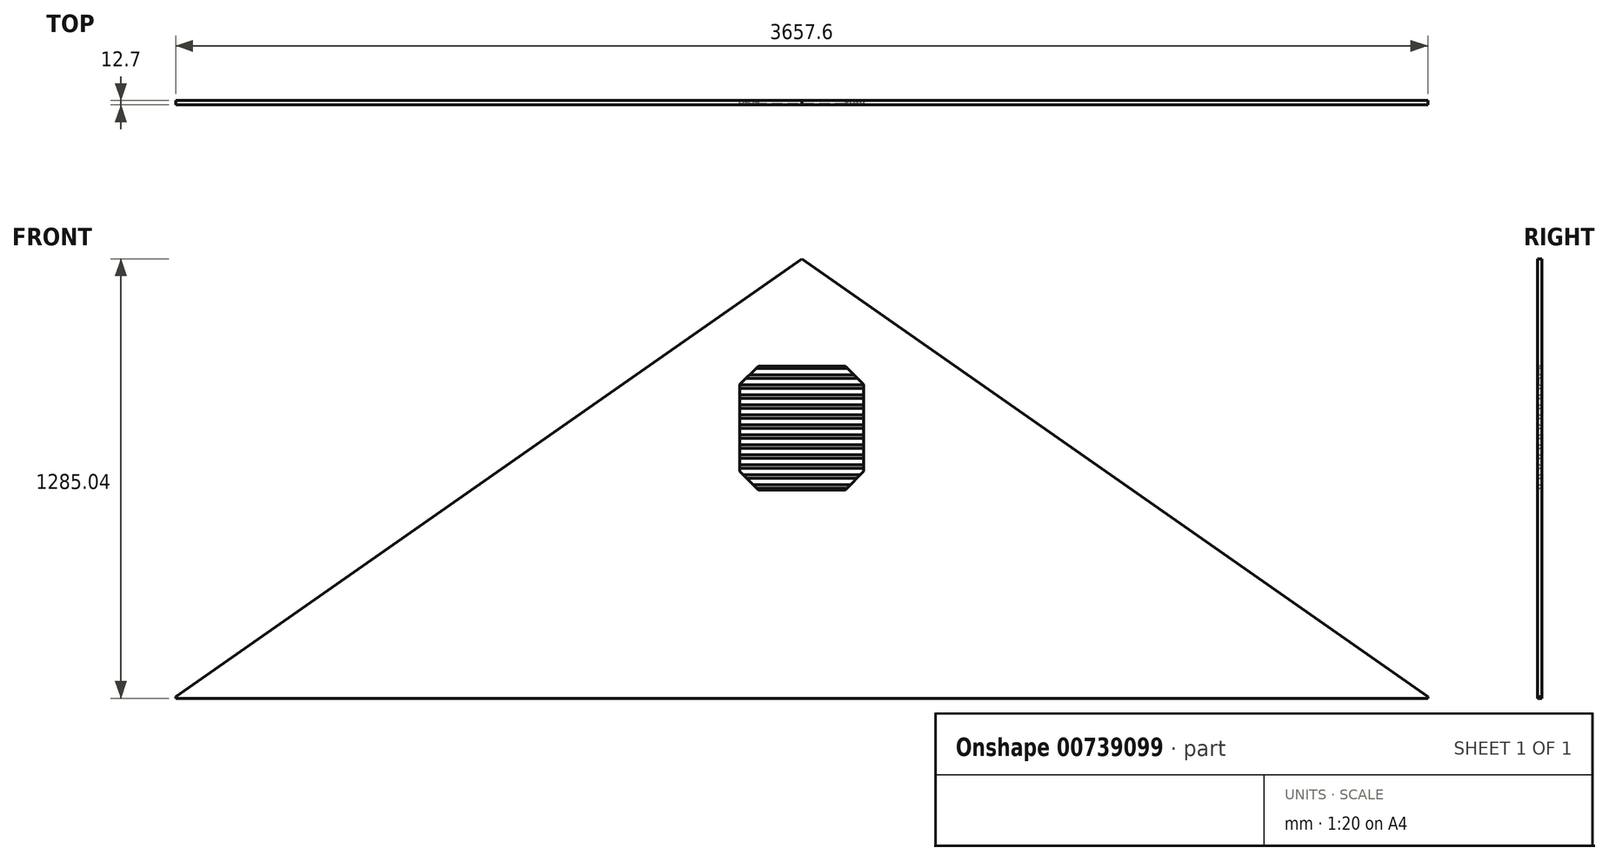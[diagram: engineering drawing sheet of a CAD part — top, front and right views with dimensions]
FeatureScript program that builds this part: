
annotation { "Feature Type Name" : "Feature", "Feature Type Description" : "" }
export const myFeature = defineFeature(function(context is Context, id is Id, definition is map)
    precondition{}
    {
        {
            var Q0;
            Q0=qCreatedBy(makeId("Front.planeOp"),FACE);
            var sketch = newSketch(context, id + "F0", { "sketchPlane" : qUnion([Q0])});
            skLineSegment(sketch, "E0", {"start": v(0, 0) * mm, "end": v(3657.6, 0) * mm});
            skLineSegment(sketch, "E1", {"start": v(3657.6, 0) * mm, "end": v(3657.6, 4.5) * mm});
            skLineSegment(sketch, "E2", {"start": v(3657.6, 4.5) * mm, "end": v(1828.8, 1285.04) * mm});
            skLineSegment(sketch, "E3", {"start": v(1828.8, 1285.04) * mm, "end": v(0, 4.5) * mm});
            skLineSegment(sketch, "E4", {"start": v(0, 4.5) * mm, "end": v(0, 0) * mm});
            skLineSegment(sketch, "E5", {"start": v(1828.8, 0) * mm, "end": v(1828.8, 1996.1) * mm});
            skSolve(sketch);
        }
        {
            var Q0;
            {var subQ4=sQuery(id+"F0.wireOp",EDGE,"E3");Q0=makeQuery(id+"F0.imprint","IMPRINT",FACE,{"disambiguationData":[TD([[makeQuery(id+"F0.imprint","IMPRINT",EDGE,{"derivedFrom":subQ4}),1.0]])]});}
            var Q1;
            {var subQ0=sQuery(id+"F0.wireOp",EDGE,"E1");Q1=makeQuery(id+"F0.imprint","IMPRINT",FACE,{"disambiguationData":[TD([[makeQuery(id+"F0.imprint","IMPRINT",EDGE,{"derivedFrom":subQ0}),1.0]])]});}
            extrude(context, id + "F1", {"entities" : qUnion([Q0, Q1]), "depth" : 12.7 * mm, "offsetDistance" : 25.4 * mm});
        }
        {
            var Q0;
            Q0=makeQuery(id+"F1.opExtrude","CAP_FACE",FACE,{"disambiguationData":[OSD([sQuery(id+"F0.wireOp",EDGE,"E0"),sQuery(id+"F0.wireOp",EDGE,"E1"),sQuery(id+"F0.wireOp",EDGE,"E2"),sQuery(id+"F0.wireOp",EDGE,"E3"),sQuery(id+"F0.wireOp",EDGE,"E4")])],"isStart":false});
            var sketch = newSketch(context, id + "F2", { "sketchPlane" : qUnion([Q0])});
            skLineSegment(sketch, "E6", {"start": v(1828.8, 1285.04) * mm, "end": v(1828.8, -385.73) * mm, "construction": true});
            skLineSegment(sketch, "E7", {"start": v(1701.8, 609.6) * mm, "end": v(1955.8, 609.6) * mm});
            skLineSegment(sketch, "E8", {"start": v(1955.8, 609.6) * mm, "end": v(2009.68, 663.48) * mm});
            skLineSegment(sketch, "E9", {"start": v(2009.68, 663.48) * mm, "end": v(2009.68, 917.48) * mm});
            skLineSegment(sketch, "E10", {"start": v(2009.68, 917.48) * mm, "end": v(1955.8, 971.36) * mm});
            skLineSegment(sketch, "E11", {"start": v(1955.8, 971.36) * mm, "end": v(1701.8, 971.36) * mm});
            skLineSegment(sketch, "E12", {"start": v(1701.8, 971.36) * mm, "end": v(1647.92, 917.48) * mm});
            skLineSegment(sketch, "E13", {"start": v(1647.92, 917.48) * mm, "end": v(1647.92, 663.48) * mm});
            skLineSegment(sketch, "E14", {"start": v(1647.92, 663.48) * mm, "end": v(1701.8, 609.6) * mm});
            skPoint(sketch, "E15", {"position": v(1828.8, 609.6) * mm});
            skLineSegment(sketch, "E16", {"start": v(1647.92, 790.48) * mm, "end": v(2046.19, 790.48) * mm});
            skSolve(sketch);
        }
        {
            var Q0;
            {var subQ1=sQuery(id+"F2.wireOp",EDGE,"E10");Q0=makeQuery(id+"F2.imprint","IMPRINT",FACE,{"disambiguationData":[TD([[makeQuery(id+"F2.imprint","IMPRINT",EDGE,{"derivedFrom":subQ1}),1.0]])]});}
            var Q1;
            Q1=makeQuery(id+"F2.imprint","IMPRINT",FACE,{"disambiguationData":[TD([[makeQuery(id+"F2.imprint","IMPRINT",EDGE,{"derivedFrom":sQuery(id+"F2.wireOp",EDGE,"E7")}),1.0]])]});
            extrude(context, id + "F3", {"entities" : qUnion([Q0, Q1]), "operationType" : NewBodyOperationType.REMOVE, "oppositeDirection" : true, "depth" : 89.66 * mm, "offsetDistance" : 25.4 * mm});
        }
        {
            var Q0;
            Q0=qCreatedBy(makeId("Front.planeOp"),FACE);
            var sketch = newSketch(context, id + "F4", { "sketchPlane" : qUnion([Q0])});
            skLineSegment(sketch, "E17.bottom", {"start": v(1524, 964.14) * mm, "end": v(2133.6, 964.14) * mm});
            skLineSegment(sketch, "E17.top", {"start": v(1524, 945.1) * mm, "end": v(2133.6, 945.1) * mm});
            skLineSegment(sketch, "E17.left", {"start": v(1524, 964.14) * mm, "end": v(1524, 945.1) * mm});
            skLineSegment(sketch, "E17.right", {"start": v(2133.6, 964.14) * mm, "end": v(2133.6, 945.1) * mm});
            skLineSegment(sketch, "E18.bottom", {"start": v(1524, 934.93) * mm, "end": v(2133.6, 934.93) * mm});
            skLineSegment(sketch, "E18.top", {"start": v(1524, 915.88) * mm, "end": v(2133.6, 915.88) * mm});
            skLineSegment(sketch, "E18.left", {"start": v(1524, 934.93) * mm, "end": v(1524, 915.88) * mm});
            skLineSegment(sketch, "E18.right", {"start": v(2133.6, 934.93) * mm, "end": v(2133.6, 915.88) * mm});
            skLineSegment(sketch, "E19.bottom", {"start": v(1524, 905.72) * mm, "end": v(2133.6, 905.72) * mm});
            skLineSegment(sketch, "E19.top", {"start": v(1524, 886.67) * mm, "end": v(2133.6, 886.67) * mm});
            skLineSegment(sketch, "E19.left", {"start": v(1524, 905.72) * mm, "end": v(1524, 886.67) * mm});
            skLineSegment(sketch, "E19.right", {"start": v(2133.6, 905.72) * mm, "end": v(2133.6, 886.67) * mm});
            skLineSegment(sketch, "E20.bottom", {"start": v(1524, 876.51) * mm, "end": v(2133.6, 876.51) * mm});
            skLineSegment(sketch, "E20.top", {"start": v(1524, 857.46) * mm, "end": v(2133.6, 857.46) * mm});
            skLineSegment(sketch, "E20.left", {"start": v(1524, 876.51) * mm, "end": v(1524, 857.46) * mm});
            skLineSegment(sketch, "E20.right", {"start": v(2133.6, 876.51) * mm, "end": v(2133.6, 857.46) * mm});
            skLineSegment(sketch, "E21.bottom", {"start": v(1524, 847.3) * mm, "end": v(2133.6, 847.3) * mm});
            skLineSegment(sketch, "E21.top", {"start": v(1524, 828.25) * mm, "end": v(2133.6, 828.25) * mm});
            skLineSegment(sketch, "E21.left", {"start": v(1524, 847.3) * mm, "end": v(1524, 828.25) * mm});
            skLineSegment(sketch, "E21.right", {"start": v(2133.6, 847.3) * mm, "end": v(2133.6, 828.25) * mm});
            skLineSegment(sketch, "E22.bottom", {"start": v(1524, 818.1) * mm, "end": v(2133.6, 818.1) * mm});
            skLineSegment(sketch, "E22.top", {"start": v(1524, 799.04) * mm, "end": v(2133.6, 799.04) * mm});
            skLineSegment(sketch, "E22.left", {"start": v(1524, 818.1) * mm, "end": v(1524, 799.04) * mm});
            skLineSegment(sketch, "E22.right", {"start": v(2133.6, 818.1) * mm, "end": v(2133.6, 799.04) * mm});
            skLineSegment(sketch, "E23.bottom", {"start": v(1524, 788.88) * mm, "end": v(2133.6, 788.88) * mm});
            skLineSegment(sketch, "E23.top", {"start": v(1524, 769.83) * mm, "end": v(2133.6, 769.83) * mm});
            skLineSegment(sketch, "E23.left", {"start": v(1524, 788.88) * mm, "end": v(1524, 769.83) * mm});
            skLineSegment(sketch, "E23.right", {"start": v(2133.6, 788.88) * mm, "end": v(2133.6, 769.83) * mm});
            skLineSegment(sketch, "E24.bottom", {"start": v(1524, 759.67) * mm, "end": v(2133.6, 759.67) * mm});
            skLineSegment(sketch, "E24.top", {"start": v(1524, 740.62) * mm, "end": v(2133.6, 740.62) * mm});
            skLineSegment(sketch, "E24.left", {"start": v(1524, 759.67) * mm, "end": v(1524, 740.62) * mm});
            skLineSegment(sketch, "E24.right", {"start": v(2133.6, 759.67) * mm, "end": v(2133.6, 740.62) * mm});
            skLineSegment(sketch, "E25.bottom", {"start": v(1524, 730.46) * mm, "end": v(2133.6, 730.46) * mm});
            skLineSegment(sketch, "E25.top", {"start": v(1524, 711.41) * mm, "end": v(2133.6, 711.41) * mm});
            skLineSegment(sketch, "E25.left", {"start": v(1524, 730.46) * mm, "end": v(1524, 711.41) * mm});
            skLineSegment(sketch, "E25.right", {"start": v(2133.6, 730.46) * mm, "end": v(2133.6, 711.41) * mm});
            skLineSegment(sketch, "E26.bottom", {"start": v(1524, 701.25) * mm, "end": v(2133.6, 701.25) * mm});
            skLineSegment(sketch, "E26.top", {"start": v(1524, 682.2) * mm, "end": v(2133.6, 682.2) * mm});
            skLineSegment(sketch, "E26.left", {"start": v(1524, 701.25) * mm, "end": v(1524, 682.2) * mm});
            skLineSegment(sketch, "E26.right", {"start": v(2133.6, 701.25) * mm, "end": v(2133.6, 682.2) * mm});
            skLineSegment(sketch, "E27.bottom", {"start": v(1524, 672.04) * mm, "end": v(2133.6, 672.04) * mm});
            skLineSegment(sketch, "E27.top", {"start": v(1524, 653) * mm, "end": v(2133.6, 653) * mm});
            skLineSegment(sketch, "E27.left", {"start": v(1524, 672.04) * mm, "end": v(1524, 653) * mm});
            skLineSegment(sketch, "E27.right", {"start": v(2133.6, 672.04) * mm, "end": v(2133.6, 653) * mm});
            skLineSegment(sketch, "E28.bottom", {"start": v(1524, 642.83) * mm, "end": v(2133.6, 642.83) * mm});
            skLineSegment(sketch, "E28.top", {"start": v(1524, 623.78) * mm, "end": v(2133.6, 623.78) * mm});
            skLineSegment(sketch, "E28.left", {"start": v(1524, 642.83) * mm, "end": v(1524, 623.78) * mm});
            skLineSegment(sketch, "E28.right", {"start": v(2133.6, 642.83) * mm, "end": v(2133.6, 623.78) * mm});
            skLineSegment(sketch, "E29.bottom", {"start": v(1524, 613.62) * mm, "end": v(2133.6, 613.62) * mm});
            skLineSegment(sketch, "E29.top", {"start": v(1524, 594.57) * mm, "end": v(2133.6, 594.57) * mm});
            skLineSegment(sketch, "E29.left", {"start": v(1524, 613.62) * mm, "end": v(1524, 594.57) * mm});
            skLineSegment(sketch, "E29.right", {"start": v(2133.6, 613.62) * mm, "end": v(2133.6, 594.57) * mm});
            skLineSegment(sketch, "E30.bottom", {"start": v(1524, 584.41) * mm, "end": v(2133.6, 584.41) * mm});
            skLineSegment(sketch, "E30.top", {"start": v(1524, 565.36) * mm, "end": v(2133.6, 565.36) * mm});
            skLineSegment(sketch, "E30.left", {"start": v(1524, 584.41) * mm, "end": v(1524, 565.36) * mm});
            skLineSegment(sketch, "E30.right", {"start": v(2133.6, 584.41) * mm, "end": v(2133.6, 565.36) * mm});
            skPoint(sketch, "E31", {"position": v(1828.8, 964.14) * mm});
            skLineSegment(sketch, "E32.0", {"start": v(3657.6, 4.5) * mm, "end": v(1828.8, 1285.04) * mm});
            skLineSegment(sketch, "E33", {"start": v(1828.8, 1285.04) * mm, "end": v(1828.8, 1012.56) * mm});
            skSolve(sketch);
        }
        {
            var Q0;
            Q0 = qSketchRegion(id + "F4", true);
            extrude(context, id + "F5", {"entities" : qUnion([Q0]), "operationType" : NewBodyOperationType.ADD, "depth" : 10.16 * mm, "offsetDistance" : 25.4 * mm});
        }
    });
